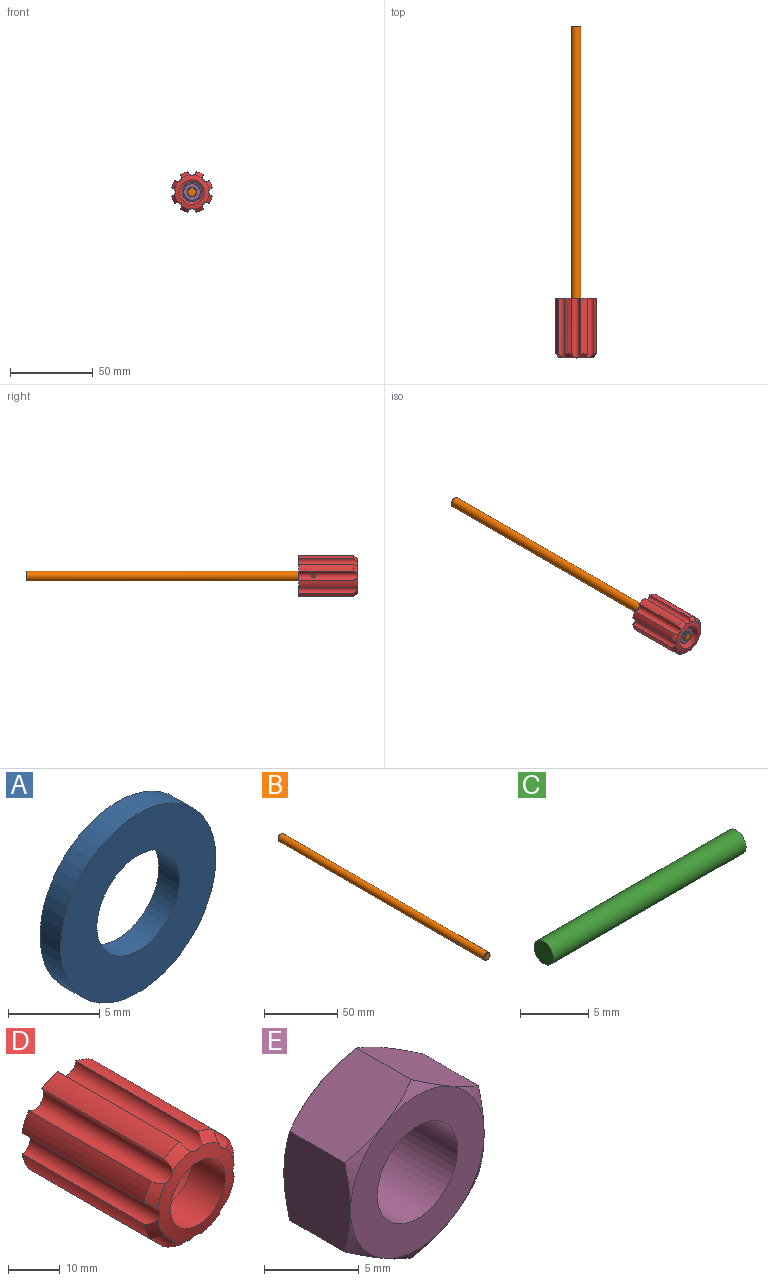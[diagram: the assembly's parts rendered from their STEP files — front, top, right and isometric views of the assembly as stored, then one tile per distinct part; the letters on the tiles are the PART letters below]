
ASSEMBLY  parts=5 mates=5
PART A: 4 faces, bbox 12x1.6x12 mm
  f0: cylinder r=3.2mm len=6.4mm, axis (0,1,0), area 32.2mm2, adj f2,f3
  f1: cylinder r=6mm len=12mm, axis (0,1,0), area 60.3mm2, adj f2,f3
  f2: plane 12x12mm, normal (0,-1,0), area 80.9mm2, adj f0,f1
  f3: plane 12x12mm, normal (0,1,0), area 80.9mm2, adj f0,f1
PART B: 6 faces, bbox 6x200x6 mm
  f0: cylinder r=3mm len=199mm, axis (0,1,0), area 3744.7mm2, adj f3,f4,f5
  f1: plane 5x5mm, normal (0,-1,0), area 19.6mm2, adj f4
  f2: plane 5x5mm, normal (0,1,0), area 19.6mm2, adj f3
  f3: cone r=3mm half-angle=45deg, axis (0,-1,0), area 12.2mm2, adj f0,f2
  f4: cone r=2.5mm half-angle=45deg, axis (0,1,0), area 12.2mm2, adj f0,f1
  f5: cylinder r=1mm len=6mm, axis (1,0,0), area 36.6mm2, adj f0
PART C: 3 faces, bbox 20x2x2 mm
  f0: cylinder r=1mm len=20mm, axis (-1,0,0), area 125.7mm2, adj f1,f2
  f1: plane 2x2mm, normal (1,0,0), area 3.1mm2, adj f0
  f2: plane 2x2mm, normal (-1,0,0), area 3.1mm2, adj f0
PART D: 31 faces, bbox 24.8x36x24.8 mm
  f0: cylinder r=3mm len=24.3mm, axis (0,-1,0), area 451.6mm2, adj f17,f18,f29,f30
  f1: cylinder r=2.5mm len=35.56mm, axis (0,-1,0), area 253.5mm2, adj f8,f9,f17,f25,f26,f28,f30
  f2: cylinder r=2.5mm len=35.56mm, axis (0,-1,0), area 253.5mm2, adj f15,f16,f17,f21,f22,f28,f29
  f3: cylinder r=2.5mm len=35.56mm, axis (0,-1,0), area 256.7mm2, adj f4,f16,f17,f22,f23,f28
  f4: cylinder r=12.5mm len=33.5mm, axis (0,-1,0), area 161.1mm2, adj f3,f5,f17,f23
  f5: cylinder r=2.5mm len=35.56mm, axis (0,-1,0), area 256.7mm2, adj f4,f6,f17,f23,f24,f28
  f6: cylinder r=12.5mm len=33.5mm, axis (0,-1,0), area 161.1mm2, adj f5,f7,f17,f24
  f7: cylinder r=2.5mm len=35.56mm, axis (0,-1,0), area 256.7mm2, adj f6,f8,f17,f24,f25,f28
  f8: cylinder r=12.5mm len=33.5mm, axis (0,-1,0), area 161.1mm2, adj f1,f7,f17,f25
  f9: cylinder r=12.5mm len=33.5mm, axis (0,-1,0), area 161.1mm2, adj f1,f10,f17,f26
  f10: cylinder r=2.5mm len=35.56mm, axis (0,-1,0), area 256.7mm2, adj f9,f11,f17,f26,f27,f28
  f11: cylinder r=12.5mm len=33.5mm, axis (0,-1,0), area 161.1mm2, adj f10,f12,f17,f27
  f12: cylinder r=2.5mm len=35.56mm, axis (0,-1,0), area 256.7mm2, adj f11,f13,f17,f20,f27,f28
  f13: cylinder r=12.5mm len=33.5mm, axis (0,-1,0), area 161.1mm2, adj f12,f14,f17,f20
  f14: cylinder r=2.5mm len=35.56mm, axis (0,-1,0), area 256.7mm2, adj f13,f15,f17,f20,f21,f28
  f15: cylinder r=12.5mm len=33.5mm, axis (0,-1,0), area 161.1mm2, adj f2,f14,f17,f21
  f16: cylinder r=12.5mm len=33.5mm, axis (0,-1,0), area 161.1mm2, adj f2,f3,f17,f22
  f17: plane 24.5x24.5mm, normal (0,1,0), area 387.4mm2, adj f0,f1,f2,f3,f4,f5,f6,f7
  f18: cone r=0mm half-angle=59deg, axis (0,-1,0), area 173.2mm2, adj f0,f19
  f19: cylinder r=7.5mm len=15mm, axis (0,-1,0), area 424.1mm2, adj f18,f28
  f20: cone r=10mm half-angle=45deg, axis (0,1,0), area 13.3mm2, adj f12,f13,f14,f28
  f21: cone r=10mm half-angle=45deg, axis (0,1,0), area 13.3mm2, adj f2,f14,f15,f28
  f22: cone r=10mm half-angle=45deg, axis (0,1,0), area 13.3mm2, adj f2,f3,f16,f28
  f23: cone r=10mm half-angle=45deg, axis (0,1,0), area 13.3mm2, adj f3,f4,f5,f28
  f24: cone r=10mm half-angle=45deg, axis (0,1,0), area 13.3mm2, adj f5,f6,f7,f28
  f25: cone r=10mm half-angle=45deg, axis (0,1,0), area 13.3mm2, adj f1,f7,f8,f28
  f26: cone r=10mm half-angle=45deg, axis (0,1,0), area 13.3mm2, adj f1,f9,f10,f28
  f27: cone r=10mm half-angle=45deg, axis (0,1,0), area 13.3mm2, adj f10,f11,f12,f28
  f28: cone r=7.5mm half-angle=80deg, axis (0,1,0), area 166.3mm2, adj f1,f2,f3,f5,f7,f10,f12,f14
  f29: cylinder r=1mm len=6.63mm, axis (0.71,0,0.71), area 45.2mm2, adj f0,f2
  f30: cylinder r=1mm len=6.63mm, axis (-0.71,0,-0.71), area 45.2mm2, adj f0,f1
PART E: 21 faces, bbox 12x5.5x12 mm
  f0: plane 10x10mm, normal (0,-1,0), area 50.3mm2, adj f2,f5,f6,f8,f10,f12,f14
  f1: plane 10x10mm, normal (0,1,0), area 50.3mm2, adj f2,f3,f4,f7,f9,f11,f13
  f2: cylinder r=3mm len=6mm, axis (0,1,0), area 94.2mm2, adj f0,f1
  f3: cone r=5mm half-angle=60deg, axis (0,-1,0), area 2.5mm2, adj f1,f15,f16
  f4: cone r=5mm half-angle=60deg, axis (0,-1,0), area 2.5mm2, adj f1,f15,f20
  f5: cone r=5mm half-angle=60deg, axis (0,1,0), area 2.5mm2, adj f0,f15,f16
  f6: cone r=5mm half-angle=60deg, axis (0,1,0), area 2.5mm2, adj f0,f15,f20
  f7: cone r=5mm half-angle=60deg, axis (0,-1,0), area 2.5mm2, adj f1,f16,f17
  f8: cone r=5mm half-angle=60deg, axis (0,1,0), area 2.5mm2, adj f0,f16,f17
  f9: cone r=5mm half-angle=60deg, axis (0,-1,0), area 2.5mm2, adj f1,f17,f18
  f10: cone r=5mm half-angle=60deg, axis (0,1,0), area 2.5mm2, adj f0,f17,f18
  f11: cone r=5mm half-angle=60deg, axis (0,-1,0), area 2.5mm2, adj f1,f18,f19
  f12: cone r=5mm half-angle=60deg, axis (0,1,0), area 2.5mm2, adj f0,f18,f19
  f13: cone r=5mm half-angle=60deg, axis (0,-1,0), area 2.5mm2, adj f1,f19,f20
  f14: cone r=5mm half-angle=60deg, axis (0,1,0), area 2.5mm2, adj f0,f19,f20
  f15: plane 5.48x5.47mm, normal (0.5,0,0.87), area 27.1mm2, adj f3,f4,f5,f6,f16,f20
  f16: plane 6.25x5.48mm, normal (1,0,0), area 27.1mm2, adj f3,f5,f7,f8,f15,f17
  f17: plane 5.48x5.47mm, normal (0.5,0,-0.87), area 27.1mm2, adj f7,f8,f9,f10,f16,f18
  f18: plane 5.48x5.47mm, normal (-0.5,0,-0.87), area 27.1mm2, adj f9,f10,f11,f12,f17,f19
  f19: plane 6.25x5.48mm, normal (-1,0,0), area 27.1mm2, adj f11,f12,f13,f14,f18,f20
  f20: plane 5.48x5.47mm, normal (-0.5,0,0.87), area 27.1mm2, adj f4,f6,f13,f14,f15,f19
PLACE A rot(axis=(0,-1,0),45deg) t=(0,-61.8,0)mm
PLACE B t=(10,36,0)mm
PLACE C t=(-4,-17,0)mm
PLACE D rot(axis=(0,1,0),45deg) t=(0,-70,0)mm
PLACE E rot(axis=(0,-1,0),45deg) t=(0,-65.1,0)mm
MATE fastened C.f0 <-> B.f5  axis (-1,0,0) through (0,-43,0)mm
MATE fastened A.f0 <-> D.f0  axis (0,1,0) through (0,-61,0)mm
MATE cylindrical D.f0 <-> B.f0  axis (0,1,0) through (0,-34,0)mm
MATE fastened E.f2 <-> A.f0  axis (0,1,0) through (0,-62.6,0)mm
MATE cylindrical D.f29 <-> C.f0  axis (-1,0,0) through (2.78,-43,0)mm
